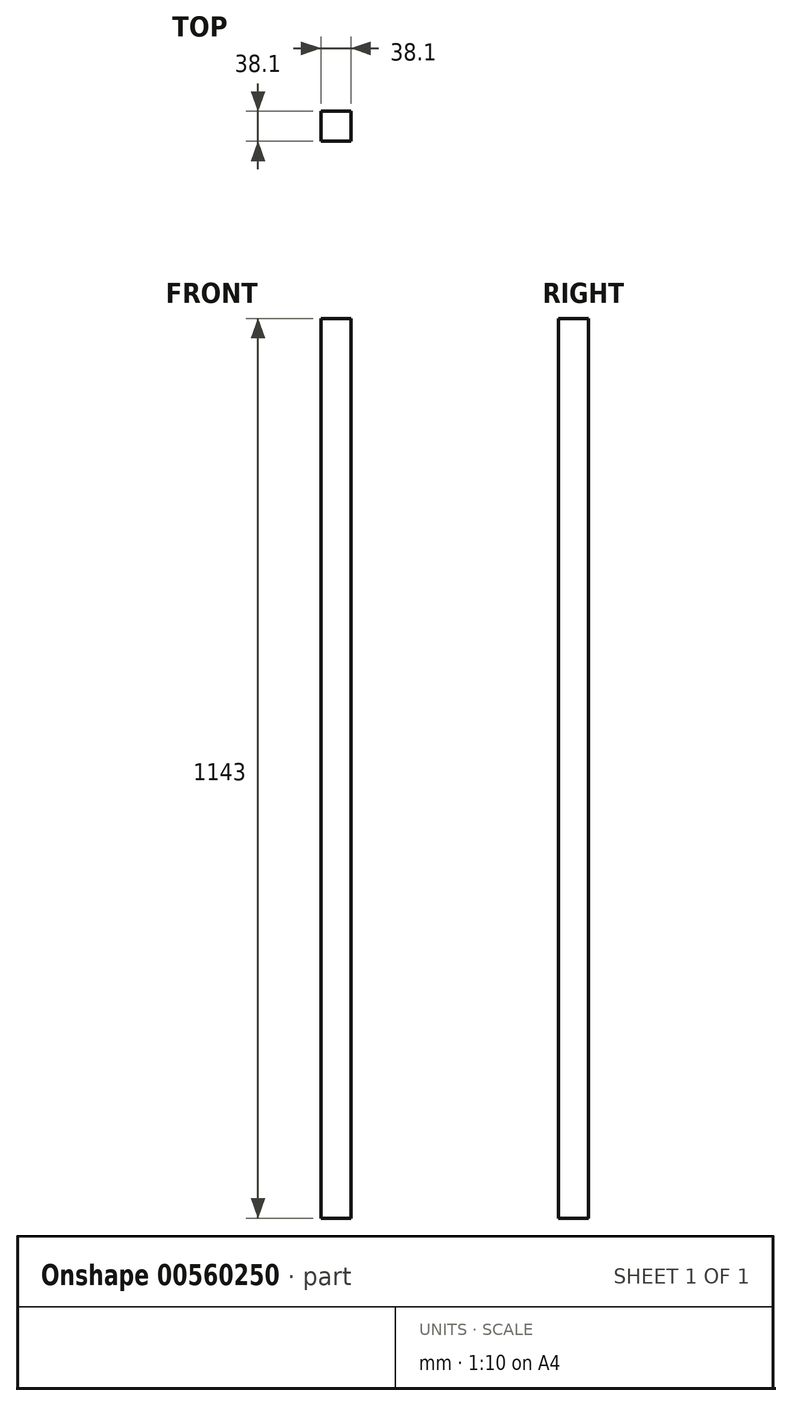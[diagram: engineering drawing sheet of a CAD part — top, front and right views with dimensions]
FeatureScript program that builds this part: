
annotation { "Feature Type Name" : "Feature", "Feature Type Description" : "" }
export const myFeature = defineFeature(function(context is Context, id is Id, definition is map)
    precondition{}
    {
        {
            var Q0;
            Q0=qCreatedBy(makeId("Front.planeOp"),FACE);
            var sketch = newSketch(context, id + "F0", { "sketchPlane" : qUnion([Q0])});
            skLineSegment(sketch, "E0.bottom", {"start": v(-19.05, 571.5) * mm, "end": v(19.05, 571.5) * mm});
            skLineSegment(sketch, "E0.top", {"start": v(-19.05, -571.5) * mm, "end": v(19.05, -571.5) * mm});
            skLineSegment(sketch, "E0.left", {"start": v(-19.05, 571.5) * mm, "end": v(-19.05, -571.5) * mm});
            skLineSegment(sketch, "E0.right", {"start": v(19.05, 571.5) * mm, "end": v(19.05, -571.5) * mm});
            skSolve(sketch);
        }
        {
            var Q0;
            Q0=makeQuery(id+"F0.imprint","IMPRINT",FACE,{"disambiguationData":[TD([[makeQuery(id+"F0.imprint","IMPRINT",EDGE,{"derivedFrom":sQuery(id+"F0.wireOp",EDGE,"E0.bottom")}),-1.0]])]});
            extrude(context, id + "F1", {"entities" : qUnion([Q0]), "depth" : 38.1 * mm, "offsetDistance" : 25.4 * mm});
        }
    });
